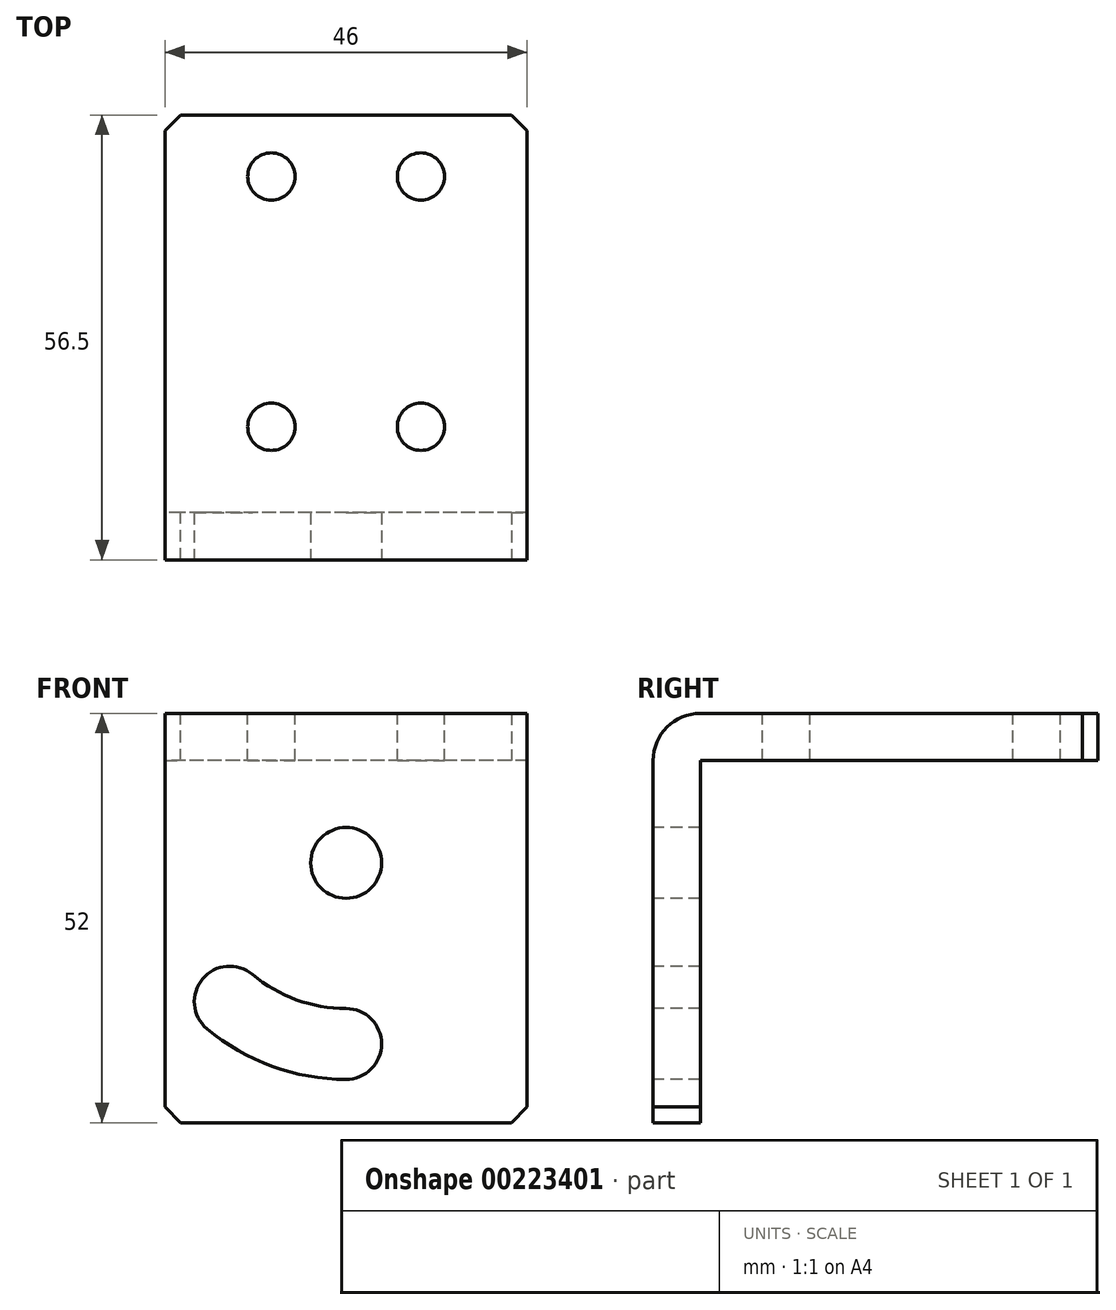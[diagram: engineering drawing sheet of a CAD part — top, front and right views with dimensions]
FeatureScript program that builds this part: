
annotation { "Feature Type Name" : "Feature", "Feature Type Description" : "" }
export const myFeature = defineFeature(function(context is Context, id is Id, definition is map)
    precondition{}
    {
        {
            var Q0;
            Q0=qCreatedBy(makeId("Right.planeOp"),FACE);
            var sketch = newSketch(context, id + "F0", { "sketchPlane" : qUnion([Q0])});
            skLineSegment(sketch, "E0", {"start": v(0, 0) * mm, "end": v(56.5, 0) * mm});
            skLineSegment(sketch, "E1", {"start": v(56.5, 0) * mm, "end": v(56.5, -6) * mm});
            skLineSegment(sketch, "E2", {"start": v(56.5, -6) * mm, "end": v(6, -6) * mm});
            skLineSegment(sketch, "E3", {"start": v(6, -6) * mm, "end": v(6, -52) * mm});
            skLineSegment(sketch, "E4", {"start": v(6, -52) * mm, "end": v(0, -52) * mm});
            skLineSegment(sketch, "E5", {"start": v(0, -52) * mm, "end": v(0, 0) * mm});
            skSolve(sketch);
        }
        {
            var Q0;
            Q0 = qSketchRegion(id + "F0", true);
            extrude(context, id + "F1", {"entities" : qUnion([Q0]), "depth" : 46 * mm});
        }
        {
            var Q0;
            Q0=makeQuery(id+"F1.opExtrude","SWEPT_FACE",FACE,{"disambiguationData":[OSD([sQuery(id+"F0.wireOp",EDGE,"E0")])]});
            var sketch = newSketch(context, id + "F2", { "sketchPlane" : qUnion([Q0])});
            skCircle(sketch, "E6", {"center": v(13.5, 16.9) * mm, "radius": 3 * mm});
            skCircle(sketch, "E7", {"center": v(32.5, 16.9) * mm, "radius": 3 * mm});
            skCircle(sketch, "E8", {"center": v(13.5, 48.7) * mm, "radius": 3 * mm});
            skCircle(sketch, "E9", {"center": v(32.5, 48.7) * mm, "radius": 3 * mm});
            skSolve(sketch);
        }
        {
            var Q0;
            Q0=sQuery(id+"F2.wireOp",VERTEX,"E6.center");
            var Q1;
            Q1=sQuery(id+"F2.wireOp",VERTEX,"E7.center");
            var Q2;
            Q2=sQuery(id+"F2.wireOp",VERTEX,"E9.center");
            var Q3;
            Q3=sQuery(id+"F2.wireOp",VERTEX,"E8.center");
            var Q4;
            Q4=makeQuery(id+"F1.opExtrude","SWEPT_BODY",BODY,{"disambiguationData":[OSD([sQuery(id+"F0.wireOp",EDGE,"E0"),sQuery(id+"F0.wireOp",EDGE,"E1"),sQuery(id+"F0.wireOp",EDGE,"E2"),sQuery(id+"F0.wireOp",EDGE,"E3"),sQuery(id+"F0.wireOp",EDGE,"E4"),sQuery(id+"F0.wireOp",EDGE,"E5")])]});
            hole(context, id + "F3", {"style" : HoleStyle.SIMPLE, "endStyle" : HoleEndStyle.THROUGH, "holeDiameter" : 6 * mm, "locations" : qUnion([Q0, Q1, Q2, Q3]), "scope" : qUnion([Q4]), "isTappedThrough" : true});
        }
        {
            var Q0;
            Q0=makeQuery(id+"F1.opExtrude","SWEPT_FACE",FACE,{"disambiguationData":[OSD([sQuery(id+"F0.wireOp",EDGE,"E5")])]});
            var sketch = newSketch(context, id + "F4", { "sketchPlane" : qUnion([Q0])});
            skCircle(sketch, "E10", {"center": v(23, -19) * mm, "radius": 4.5 * mm});
            skArc(sketch, "E11", {"start": v(11.1, -33.17) * mm, "mid": v(16.67, -36.38) * mm, "end": v(23, -37.5) * mm});
            skArc(sketch, "E12", {"start": v(5.32, -40.07) * mm, "mid": v(13.6, -44.84) * mm, "end": v(23, -46.5) * mm});
            skArc(sketch, "E13", {"start": v(23, -46.5) * mm, "mid": v(27.5, -42) * mm, "end": v(23, -37.5) * mm});
            skArc(sketch, "E14", {"start": v(11.1, -33.17) * mm, "mid": v(4.77, -33.73) * mm, "end": v(5.32, -40.07) * mm});
            skSolve(sketch);
        }
        {
            var Q0;
            Q0=makeQuery(id+"F1.opExtrude","SWEPT_EDGE",EDGE,{"disambiguationData":[OSD([sQuery(id+"F0.wireOp",EDGE,"E0"),sQuery(id+"F0.wireOp",EDGE,"E5")])]});
            fillet(context, id + "F5", {"entities" : qUnion([Q0]), "radius" : 6 * mm, "tangentPropagation" : true, "allowEdgeOverflow" : false});
        }
        {
            var Q0;
            Q0=makeQuery(id+"F1.opExtrude","CAP_EDGE",EDGE,{"disambiguationData":[OSD([sQuery(id+"F0.wireOp",EDGE,"E1")])],"isStart":false});
            var Q1;
            Q1=makeQuery(id+"F1.opExtrude","CAP_EDGE",EDGE,{"disambiguationData":[OSD([sQuery(id+"F0.wireOp",EDGE,"E1")])],"isStart":true});
            var Q2;
            Q2=makeQuery(id+"F1.opExtrude","CAP_EDGE",EDGE,{"disambiguationData":[OSD([sQuery(id+"F0.wireOp",EDGE,"E4")])],"isStart":true});
            var Q3;
            Q3=makeQuery(id+"F1.opExtrude","CAP_EDGE",EDGE,{"disambiguationData":[OSD([sQuery(id+"F0.wireOp",EDGE,"E4")])],"isStart":false});
            chamfer(context, id + "F6", {"entities" : qUnion([Q0, Q1, Q2, Q3]), "width" : 2 * mm, "tangentPropagation" : true});
        }
        {
            var Q0;
            Q0 = qSketchRegion(id + "F4", true);
            extrude(context, id + "F7", {"entities" : qUnion([Q0]), "operationType" : NewBodyOperationType.REMOVE, "oppositeDirection" : true, "depth" : 25 * mm});
        }
    });
